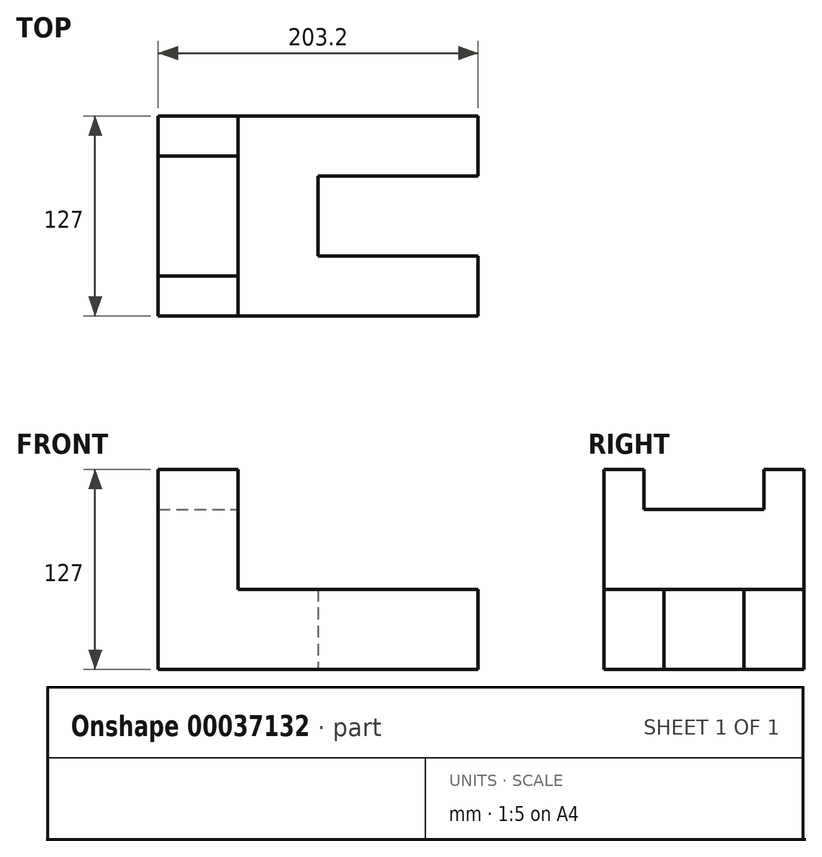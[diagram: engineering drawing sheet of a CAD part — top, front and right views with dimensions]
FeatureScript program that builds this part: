
annotation { "Feature Type Name" : "Feature", "Feature Type Description" : "" }
export const myFeature = defineFeature(function(context is Context, id is Id, definition is map)
    precondition{}
    {
        {
            var Q0;
            Q0=qCreatedBy(makeId("Top.planeOp"),FACE);
            var sketch = newSketch(context, id + "F0", { "sketchPlane" : qUnion([Q0])});
            skLineSegment(sketch, "E0", {"start": v(-203.2, 103.12) * mm, "end": v(-203.2, -23.88) * mm});
            skLineSegment(sketch, "E1", {"start": v(-203.2, 103.12) * mm, "end": v(0, 103.12) * mm});
            skLineSegment(sketch, "E2", {"start": v(-203.2, -23.88) * mm, "end": v(0, -23.88) * mm});
            skLineSegment(sketch, "E3", {"start": v(0, 103.12) * mm, "end": v(0, 65.02) * mm});
            skLineSegment(sketch, "E4", {"start": v(0, -23.88) * mm, "end": v(0, 14.22) * mm});
            skLineSegment(sketch, "E5", {"start": v(0, 14.22) * mm, "end": v(-101.6, 14.22) * mm});
            skLineSegment(sketch, "E6", {"start": v(0, 65.02) * mm, "end": v(-101.6, 65.02) * mm});
            skLineSegment(sketch, "E7", {"start": v(-101.6, 14.22) * mm, "end": v(-101.6, 65.02) * mm});
            skSolve(sketch);
        }
        {
            var Q0;
            Q0=makeQuery(id+"F0.imprint","IMPRINT",FACE,{"disambiguationData":[TD([[makeQuery(id+"F0.imprint","IMPRINT",EDGE,{"derivedFrom":sQuery(id+"F0.wireOp",EDGE,"E0")}),1.0]])]});
            extrude(context, id + "F1", {"entities" : qUnion([Q0]), "depth" : 50.8 * mm});
        }
        {
            var Q0;
            Q0=makeQuery(id+"F1.opExtrude","CAP_FACE",FACE,{"disambiguationData":[OSD([sQuery(id+"F0.wireOp",EDGE,"E0"),sQuery(id+"F0.wireOp",EDGE,"E1"),sQuery(id+"F0.wireOp",EDGE,"E2"),sQuery(id+"F0.wireOp",EDGE,"E3"),sQuery(id+"F0.wireOp",EDGE,"E4"),sQuery(id+"F0.wireOp",EDGE,"E5"),sQuery(id+"F0.wireOp",EDGE,"E6"),sQuery(id+"F0.wireOp",EDGE,"E7")])],"isStart":false});
            var sketch = newSketch(context, id + "F2", { "sketchPlane" : qUnion([Q0])});
            skLineSegment(sketch, "E8", {"start": v(-203.2, 103.12) * mm, "end": v(-203.2, -23.88) * mm});
            skLineSegment(sketch, "E9", {"start": v(-203.2, -23.88) * mm, "end": v(-152.4, -23.88) * mm});
            skLineSegment(sketch, "E10", {"start": v(-152.4, -23.88) * mm, "end": v(-152.4, 103.12) * mm});
            skLineSegment(sketch, "E11", {"start": v(-152.4, 103.12) * mm, "end": v(-203.2, 103.12) * mm});
            skSolve(sketch);
        }
        {
            var Q0;
            Q0=makeQuery(id+"F2.imprint","IMPRINT",FACE,{"disambiguationData":[TD([[makeQuery(id+"F2.imprint","IMPRINT",EDGE,{"derivedFrom":sQuery(id+"F2.wireOp",EDGE,"E8")}),1.0]])]});
            extrude(context, id + "F3", {"entities" : qUnion([Q0]), "operationType" : NewBodyOperationType.ADD, "depth" : 76.2 * mm});
        }
        {
            var Q0;
            Q0=makeQuery(id+"F3.opExtrude","SWEPT_FACE",FACE,{"disambiguationData":[OSD([sQuery(id+"F2.wireOp",EDGE,"E10")])]});
            var sketch = newSketch(context, id + "F4", { "sketchPlane" : qUnion([Q0])});
            skLineSegment(sketch, "E12", {"start": v(-23.88, 127) * mm, "end": v(1.52, 127) * mm});
            skLineSegment(sketch, "E13", {"start": v(1.52, 127) * mm, "end": v(1.52, 101.6) * mm});
            skLineSegment(sketch, "E14", {"start": v(1.52, 101.6) * mm, "end": v(77.72, 101.6) * mm});
            skLineSegment(sketch, "E15", {"start": v(77.72, 101.6) * mm, "end": v(77.72, 127) * mm});
            skLineSegment(sketch, "E16", {"start": v(77.72, 127) * mm, "end": v(1.52, 127) * mm});
            skSolve(sketch);
        }
        {
            var Q0;
            Q0=makeQuery(id+"F4.imprint","IMPRINT",FACE,{"disambiguationData":[TD([[makeQuery(id+"F4.imprint","IMPRINT",EDGE,{"derivedFrom":sQuery(id+"F4.wireOp",EDGE,"E13")}),1.0]])]});
            extrude(context, id + "F5", {"entities" : qUnion([Q0]), "operationType" : NewBodyOperationType.REMOVE, "oppositeDirection" : true, "depth" : 50.8 * mm});
        }
    });
